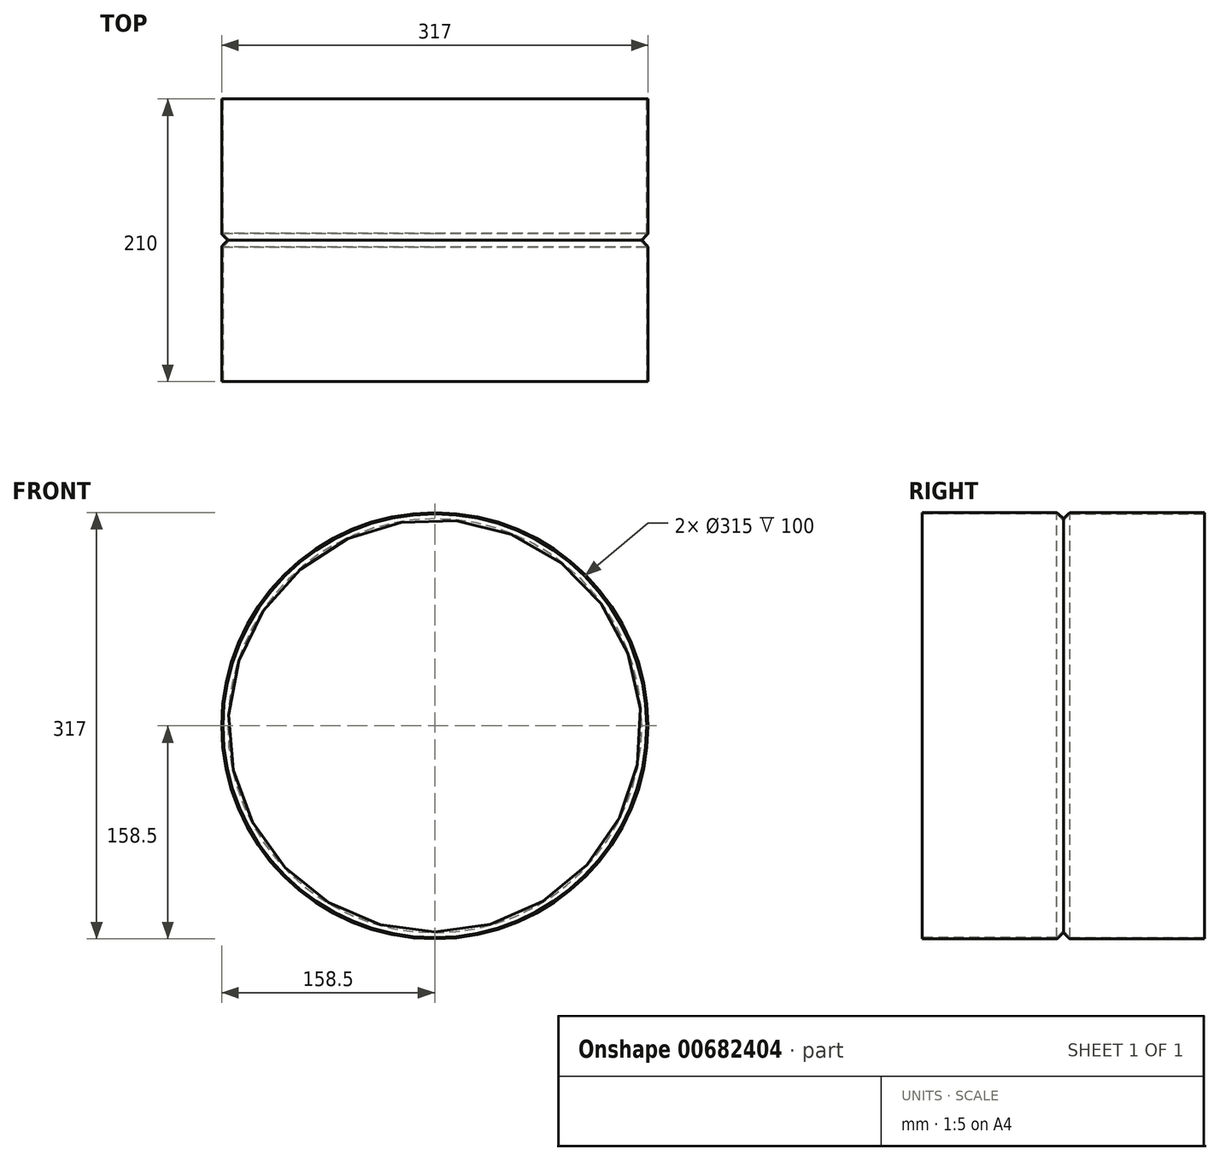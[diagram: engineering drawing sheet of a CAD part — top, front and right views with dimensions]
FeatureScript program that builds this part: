
annotation { "Feature Type Name" : "Feature", "Feature Type Description" : "" }
export const myFeature = defineFeature(function(context is Context, id is Id, definition is map)
    precondition{}
    {
        {
            var Q0;
            Q0=qCreatedBy(makeId("Front.planeOp"),FACE);
            var sketch = newSketch(context, id + "F0", { "sketchPlane" : qUnion([Q0])});
            skCircle(sketch, "E0", {"center": v(0, 0) * mm, "radius": 157.5 * mm});
            skSolve(sketch);
        }
        {
            var Q0;
            Q0 = qSketchRegion(id + "F0", true);
            extrude(context, id + "F1", {"entities" : qUnion([Q0]), "depth" : 100 * mm, "offsetDistance" : 25 * mm});
        }
        {
            var Q0;
            Q0=makeQuery(id+"F1.opExtrude","CAP_FACE",FACE,{"disambiguationData":[OSD([sQuery(id+"F0.wireOp",EDGE,"E0")])],"isStart":false});
            var sketch = newSketch(context, id + "F2", { "sketchPlane" : qUnion([Q0])});
            skCircle(sketch, "E1", {"center": v(0, 0) * mm, "radius": 157.5 * mm});
            skSolve(sketch);
        }
        {
            var Q0;
            Q0=makeQuery(id+"F2.imprint","IMPRINT",FACE,{"disambiguationData":[TD([[makeQuery(id+"F2.imprint","IMPRINT",EDGE,{"derivedFrom":sQuery(id+"F2.wireOp",EDGE,"E1")}),1.0]])]});
            extrude(context, id + "F3", {"entities" : qUnion([Q0]), "operationType" : NewBodyOperationType.ADD, "depth" : 5 * mm, "offsetDistance" : 25 * mm, "hasDraft" : true, "draftAngle" : 45 * degree, "draftPullDirection" : true});
        }
        {
            var Q0;
            Q0=makeQuery(id+"F3.opExtrude","CAP_FACE",FACE,{"disambiguationData":[OSD([sQuery(id+"F2.wireOp",EDGE,"E1")])],"isStart":false});
            var Q1;
            Q1=makeQuery(id+"F1.opExtrude","CAP_FACE",FACE,{"disambiguationData":[OSD([sQuery(id+"F0.wireOp",EDGE,"E0")])],"isStart":true});
            shell(context, id + "F4", {"entities" : qUnion([Q0, Q1]), "thickness" : 1 * mm, "oppositeDirection" : true});
        }
        {
            var Q0;
            Q0=makeQuery(id+"F1.opExtrude","SWEPT_BODY",BODY,{"disambiguationData":[OSD([sQuery(id+"F0.wireOp",EDGE,"E0")])]});
            var Q1;
            Q1=makeQuery(id+"F3.opExtrude","CAP_FACE",FACE,{"disambiguationData":[OSD([sQuery(id+"F2.wireOp",EDGE,"E1")])],"isStart":false});
            mirror(context, id + "F5", {"operationType" : NewBodyOperationType.ADD, "entities" : qUnion([Q0]), "mirrorPlane" : qUnion([Q1])});
        }
        {
            var Q0;
            {var subQ0=makeQuery(id+"F4.opShell","OFFSET_EDGE",EDGE,{"disambiguationData":[OSD([sQuery(id+"F2.wireOp",EDGE,"E1")])]});Q0=makeQuery(id+"F5.boolean.opBoolean","MERGE",EDGE,{"derivedFrom":[subQ0,makeQuery(id+"F5.opPattern","COPY",EDGE,{"derivedFrom":subQ0,"instanceName":"1"})]});}
            fillet(context, id + "F6", {"entities" : qUnion([Q0]), "radius" : 2 * mm, "tangentPropagation" : true, "allowEdgeOverflow" : false});
        }
        {
            var Q0;
            Q0=makeQuery(id+"F5.opPattern","COPY",EDGE,{"derivedFrom":makeQuery(id+"F3.boolean.opBoolean","MERGE",EDGE,{"derivedFrom":[makeQuery(id+"F1.opExtrude","CAP_EDGE",EDGE,{"disambiguationData":[OSD([sQuery(id+"F0.wireOp",EDGE,"E0")])],"isStart":false}),makeQuery(id+"F3.opExtrude","CAP_EDGE",EDGE,{"disambiguationData":[OSD([sQuery(id+"F2.wireOp",EDGE,"E1")])],"isStart":true})]}),"instanceName":"1"});
            var Q1;
            Q1=makeQuery(id+"F3.boolean.opBoolean","MERGE",EDGE,{"derivedFrom":[makeQuery(id+"F1.opExtrude","CAP_EDGE",EDGE,{"disambiguationData":[OSD([sQuery(id+"F0.wireOp",EDGE,"E0")])],"isStart":false}),makeQuery(id+"F3.opExtrude","CAP_EDGE",EDGE,{"disambiguationData":[OSD([sQuery(id+"F2.wireOp",EDGE,"E1")])],"isStart":true})]});
            fillet(context, id + "F7", {"entities" : qUnion([Q0, Q1]), "radius" : 3 * mm, "tangentPropagation" : true, "allowEdgeOverflow" : false});
        }
    });
